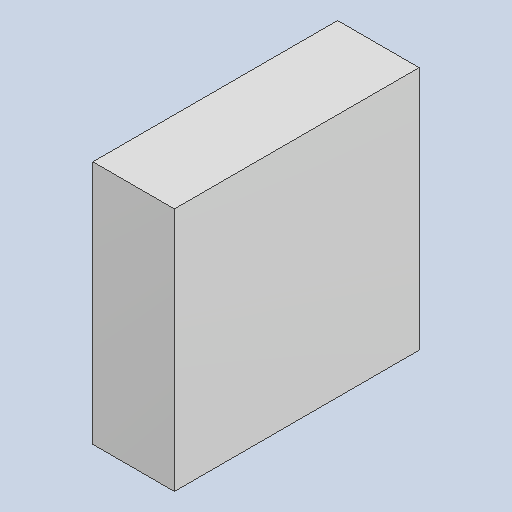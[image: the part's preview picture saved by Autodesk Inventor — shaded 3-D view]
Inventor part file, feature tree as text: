
AUTODESK INVENTOR PART (.ipt)
format: ipt  version: 2023.4 (Build 274418000, 418)  size: 81,408 bytes
history: native  units: mm
features: extrude x1
ambient origin geometry x8: Origin, YZ Plane, XZ Plane, XY Plane, X Axis, Y Axis, Z Axis, Center Point
bodies: Solid1 (feature_tree)
feature tree (1):
  extrude  "Extruded_6"  [1 undecoded]
note: 1 required parameter value undecoded (feature->parameter linkage not recoverable at this tier; creation-order binding heuristic only, values carry confidence <= 0.55)
